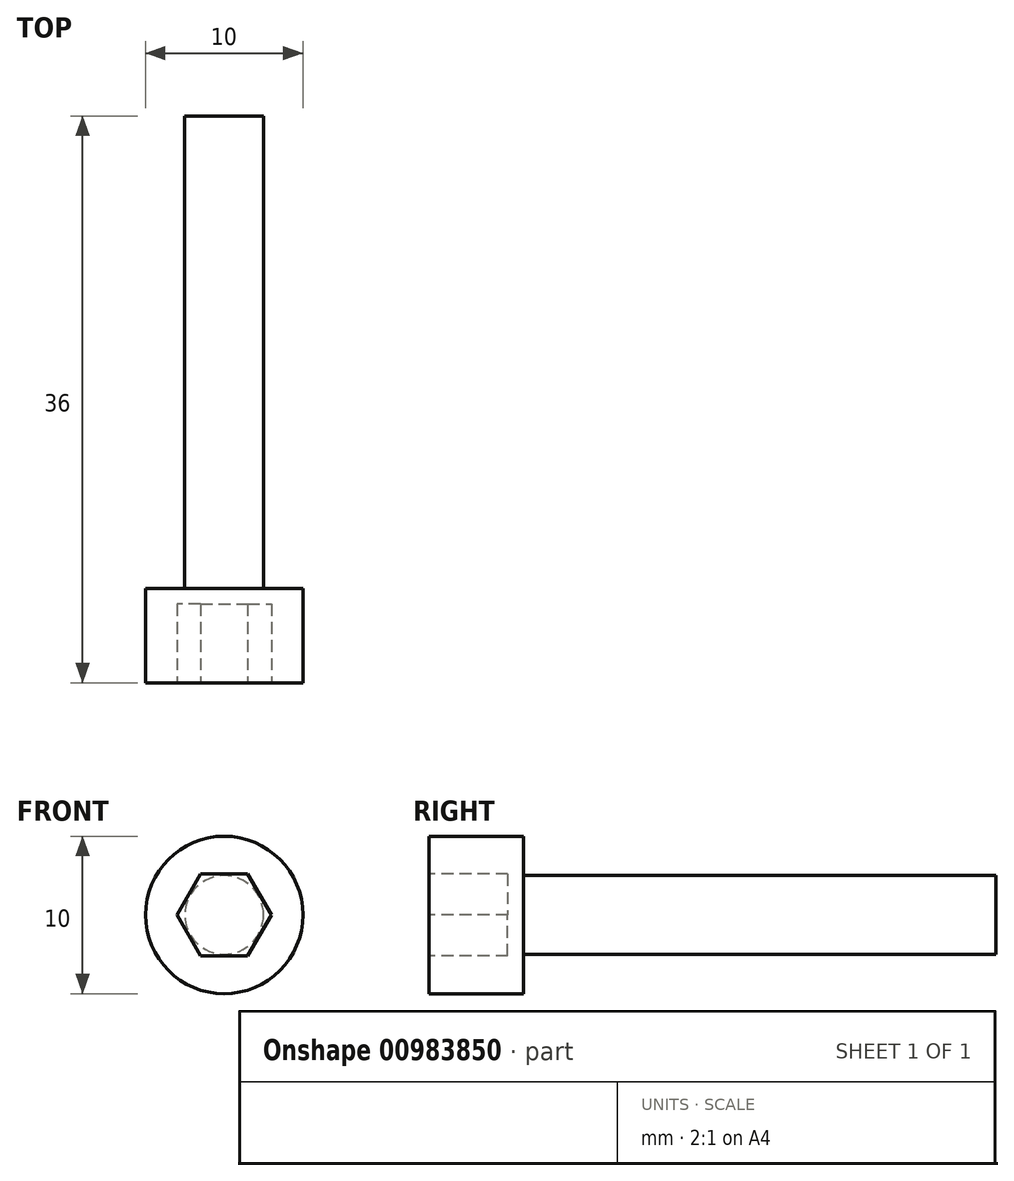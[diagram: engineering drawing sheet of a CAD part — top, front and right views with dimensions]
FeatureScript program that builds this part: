
annotation { "Feature Type Name" : "Feature", "Feature Type Description" : "" }
export const myFeature = defineFeature(function(context is Context, id is Id, definition is map)
    precondition{}
    {
        {
            var Q0;
            Q0=qCreatedBy(makeId("Front.planeOp"),FACE);
            var sketch = newSketch(context, id + "F0", { "sketchPlane" : qUnion([Q0])});
            skCircle(sketch, "E0", {"center": v(0, 0) * mm, "radius": 2.5 * mm});
            skSolve(sketch);
        }
        {
            var Q0;
            Q0=makeQuery(id+"F0.imprint","IMPRINT",FACE,{"disambiguationData":[TD([[makeQuery(id+"F0.imprint","IMPRINT",EDGE,{"derivedFrom":sQuery(id+"F0.wireOp",EDGE,"E0")}),1.0]])]});
            extrude(context, id + "F1", {"entities" : qUnion([Q0]), "oppositeDirection" : true, "depth" : 30 * mm, "offsetDistance" : 25 * mm});
        }
        {
            var Q0;
            Q0=makeQuery(id+"F1.opExtrude","CAP_FACE",FACE,{"disambiguationData":[OSD([sQuery(id+"F0.wireOp",EDGE,"E0")])],"isStart":true});
            cPlane(context, id + "F2", {"entities" : qUnion([Q0]), "cplaneType" : CPlaneType.OFFSET, "offset" : 0 * mm, "width" : 150 * mm, "height" : 150 * mm});
        }
        {
            var Q0;
            Q0=qCreatedBy(id+"F2.planeOp",FACE);
            var sketch = newSketch(context, id + "F3", { "sketchPlane" : qUnion([Q0])});
            skCircle(sketch, "E1", {"center": v(0, 0) * mm, "radius": 5 * mm});
            skSolve(sketch);
        }
        {
            var Q0;
            Q0=makeQuery(id+"F3.imprint","IMPRINT",FACE,{"disambiguationData":[TD([[makeQuery(id+"F3.imprint","IMPRINT",EDGE,{"derivedFrom":sQuery(id+"F3.wireOp",EDGE,"E1")}),1.0]])]});
            extrude(context, id + "F4", {"entities" : qUnion([Q0]), "operationType" : NewBodyOperationType.ADD, "depth" : 6 * mm, "offsetDistance" : 25 * mm});
        }
        {
            var Q0;
            Q0=makeQuery(id+"F4.opExtrude","CAP_FACE",FACE,{"disambiguationData":[OSD([sQuery(id+"F3.wireOp",EDGE,"E1")])],"isStart":false});
            cPlane(context, id + "F5", {"entities" : qUnion([Q0]), "cplaneType" : CPlaneType.OFFSET, "offset" : 0 * mm, "width" : 150 * mm, "height" : 150 * mm});
        }
        {
            var Q0;
            Q0=qCreatedBy(id+"F5.planeOp",FACE);
            var sketch = newSketch(context, id + "F6", { "sketchPlane" : qUnion([Q0])});
            skLineSegment(sketch, "E2", {"start": v(-1.5, 2.6) * mm, "end": v(1.5, 2.6) * mm});
            skLineSegment(sketch, "E3", {"start": v(1.5, 2.6) * mm, "end": v(3, 0) * mm});
            skLineSegment(sketch, "E4", {"start": v(1.5, -2.6) * mm, "end": v(3, 0) * mm});
            skLineSegment(sketch, "E5", {"start": v(-1.5, 2.6) * mm, "end": v(-3, 0) * mm});
            skLineSegment(sketch, "E6", {"start": v(-1.5, -2.6) * mm, "end": v(-3, 0) * mm});
            skLineSegment(sketch, "E7", {"start": v(-1.5, -2.6) * mm, "end": v(1.5, -2.6) * mm});
            skPoint(sketch, "E8.MirrorCS.start.orphan", {"position": v(0, 0) * mm});
            skSolve(sketch);
        }
        {
            var Q0;
            Q0=makeQuery(id+"F6.imprint","IMPRINT",FACE,{"disambiguationData":[TD([[makeQuery(id+"F6.imprint","IMPRINT",EDGE,{"derivedFrom":sQuery(id+"F6.wireOp",EDGE,"E2")}),-1.0]])]});
            extrude(context, id + "F7", {"entities" : qUnion([Q0]), "operationType" : NewBodyOperationType.REMOVE, "oppositeDirection" : true, "depth" : 5 * mm, "offsetDistance" : 25 * mm});
        }
    });
